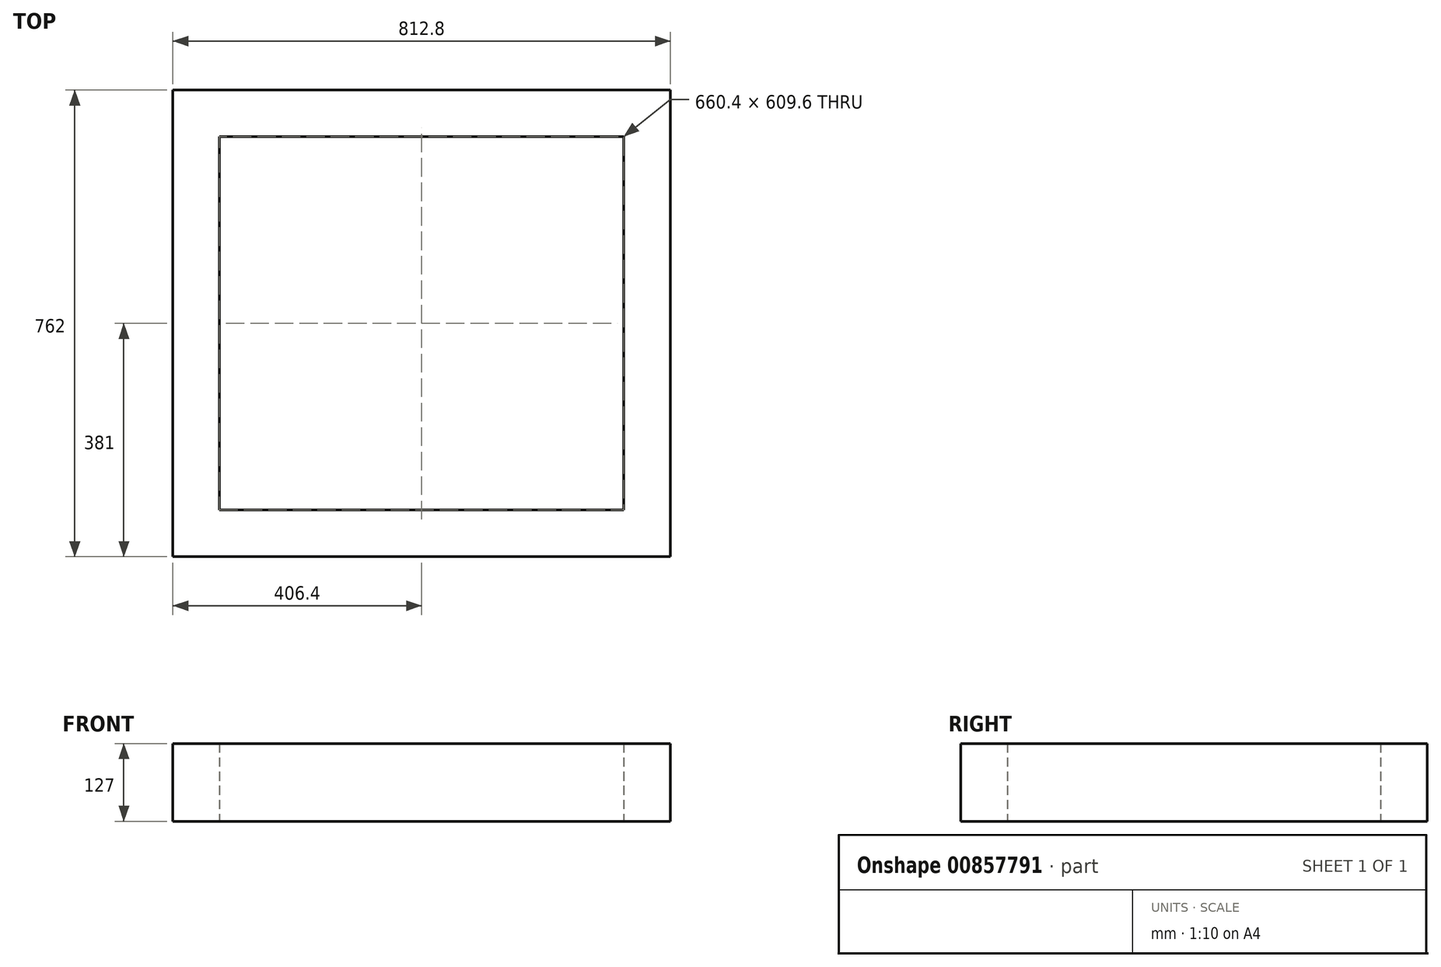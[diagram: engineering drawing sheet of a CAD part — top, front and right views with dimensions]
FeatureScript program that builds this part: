
annotation { "Feature Type Name" : "Feature", "Feature Type Description" : "" }
export const myFeature = defineFeature(function(context is Context, id is Id, definition is map)
    precondition{}
    {
        {
            var Q0;
            Q0=qCreatedBy(makeId("Top.planeOp"),FACE);
            var sketch = newSketch(context, id + "F0", { "sketchPlane" : qUnion([Q0])});
            skLineSegment(sketch, "E0.bottom", {"start": v(0, 0) * mm, "end": v(0, 0) * mm});
            skLineSegment(sketch, "E0.top", {"start": v(0, 0) * mm, "end": v(0, 0) * mm});
            skLineSegment(sketch, "E0.left", {"start": v(0, 0) * mm, "end": v(0, 0) * mm});
            skLineSegment(sketch, "E0.right", {"start": v(0, 0) * mm, "end": v(0, 0) * mm});
            skPoint(sketch, "E0.middle", {"position": v(0, 0) * mm});
            skLineSegment(sketch, "E1.bottom", {"start": v(-330.2, 304.8) * mm, "end": v(330.2, 304.8) * mm});
            skLineSegment(sketch, "E1.top", {"start": v(-330.2, -304.8) * mm, "end": v(330.2, -304.8) * mm});
            skLineSegment(sketch, "E1.left", {"start": v(-330.2, 304.8) * mm, "end": v(-330.2, -304.8) * mm});
            skLineSegment(sketch, "E1.right", {"start": v(330.2, 304.8) * mm, "end": v(330.2, -304.8) * mm});
            skLineSegment(sketch, "E2.bottom", {"start": v(-406.4, 381) * mm, "end": v(406.4, 381) * mm});
            skLineSegment(sketch, "E2.top", {"start": v(-406.4, -381) * mm, "end": v(406.4, -381) * mm});
            skLineSegment(sketch, "E2.left", {"start": v(-406.4, 381) * mm, "end": v(-406.4, -381) * mm});
            skLineSegment(sketch, "E2.right", {"start": v(406.4, 381) * mm, "end": v(406.4, -381) * mm});
            skSolve(sketch);
        }
        {
            var Q0;
            Q0=makeQuery(id+"F0.imprint","IMPRINT",FACE,{"disambiguationData":[TD([[makeQuery(id+"F0.imprint","IMPRINT",EDGE,{"derivedFrom":sQuery(id+"F0.wireOp",EDGE,"E1.bottom")}),1.0]])]});
            extrude(context, id + "F1", {"entities" : qUnion([Q0]), "depth" : 127 * mm, "offsetDistance" : 25.4 * mm});
        }
    });
